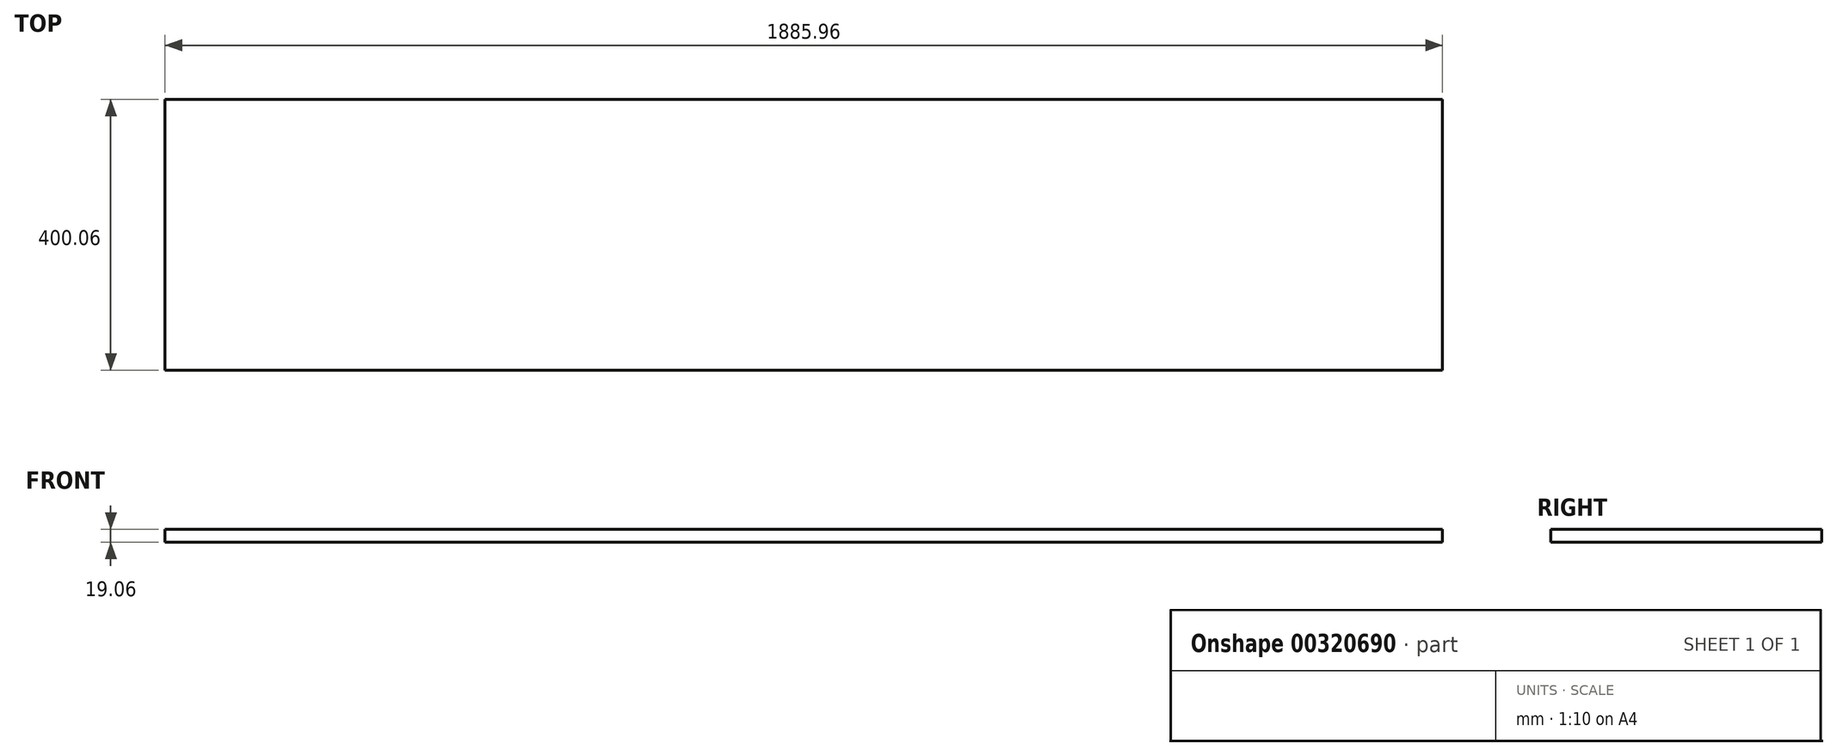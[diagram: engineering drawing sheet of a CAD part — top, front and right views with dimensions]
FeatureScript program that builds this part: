
annotation { "Feature Type Name" : "Feature", "Feature Type Description" : "" }
export const myFeature = defineFeature(function(context is Context, id is Id, definition is map)
    precondition{}
    {
        {
            var Q0;
            Q0=qCreatedBy(makeId("Front.planeOp"),FACE);
            var sketch = newSketch(context, id + "F0", { "sketchPlane" : qUnion([Q0])});
            skLineSegment(sketch, "E0.bottom", {"start": v(-942.98, -9.53) * mm, "end": v(942.98, -9.53) * mm});
            skLineSegment(sketch, "E0.top", {"start": v(-942.98, 9.53) * mm, "end": v(942.98, 9.53) * mm});
            skLineSegment(sketch, "E0.left", {"start": v(-942.98, -9.53) * mm, "end": v(-942.98, 9.53) * mm});
            skLineSegment(sketch, "E0.right", {"start": v(942.98, -9.53) * mm, "end": v(942.98, 9.53) * mm});
            skPoint(sketch, "E0.middle", {"position": v(0, 0) * mm});
            skSolve(sketch);
        }
        {
            var Q0;
            Q0 = qSketchRegion(id + "F0", true);
            extrude(context, id + "F1", {"entities" : qUnion([Q0]), "depth" : 400.05 * mm, "symmetric" : true});
        }
    });
